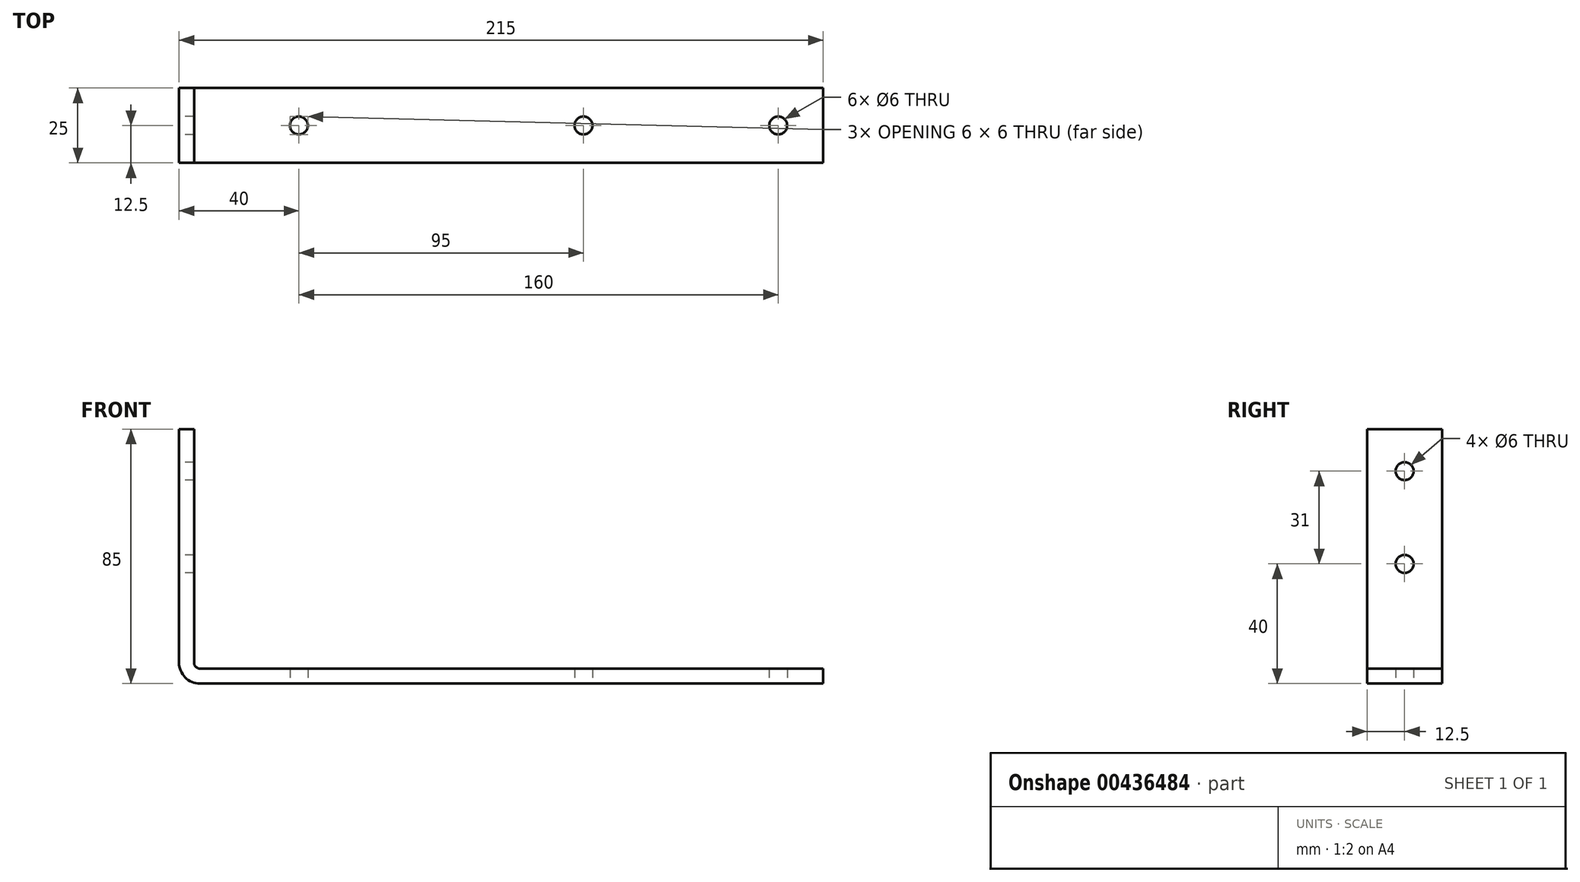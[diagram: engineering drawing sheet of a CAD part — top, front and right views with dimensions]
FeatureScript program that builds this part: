
annotation { "Feature Type Name" : "Feature", "Feature Type Description" : "" }
export const myFeature = defineFeature(function(context is Context, id is Id, definition is map)
    precondition{}
    {
        {
            var Q0;
            Q0=qCreatedBy(makeId("Front.planeOp"),FACE);
            var sketch = newSketch(context, id + "F0", { "sketchPlane" : qUnion([Q0])});
            skLineSegment(sketch, "E0.bottom", {"start": v(0, 85) * mm, "end": v(5, 85) * mm});
            skLineSegment(sketch, "E0.top", {"start": v(7, 0) * mm, "end": v(215, 0) * mm});
            skLineSegment(sketch, "E0.left", {"start": v(0, 85) * mm, "end": v(0, 7) * mm});
            skLineSegment(sketch, "E0.right", {"start": v(215, 5) * mm, "end": v(215, 0) * mm});
            skLineSegment(sketch, "E1.top", {"start": v(7, 5) * mm, "end": v(215, 5) * mm});
            skLineSegment(sketch, "E1.left", {"start": v(5, 85) * mm, "end": v(5, 7) * mm});
            skPoint(sketch, "E2.visualSharp", {"position": v(0, 0) * mm});
            skArc(sketch, "E2.filletArc", {"start": v(0, 7) * mm, "mid": v(2.05, 2.05) * mm, "end": v(7, 0) * mm});
            skPoint(sketch, "E3.visualSharp", {"position": v(5, 5) * mm});
            skArc(sketch, "E3.filletArc", {"start": v(5, 7) * mm, "mid": v(5.59, 5.59) * mm, "end": v(7, 5) * mm});
            skSolve(sketch);
        }
        {
            var Q0;
            Q0 = qSketchRegion(id + "F0", true);
            extrude(context, id + "F1", {"entities" : qUnion([Q0]), "depth" : 12.5 * mm, "hasSecondDirection" : true, "secondDirectionOppositeDirection" : true, "secondDirectionDepth" : 12.5 * mm});
        }
        {
            var Q0;
            Q0=makeQuery(id+"F1.opExtrude","SWEPT_FACE",FACE,{"disambiguationData":[OSD([sQuery(id+"F0.wireOp",EDGE,"E0.top")])]});
            var sketch = newSketch(context, id + "F2", { "sketchPlane" : qUnion([Q0])});
            skPoint(sketch, "E4", {"position": v(40, 0) * mm});
            skPoint(sketch, "E4.positionSnap0", {"position": v(7, 0) * mm});
            skPoint(sketch, "E5", {"position": v(135, 0) * mm});
            skPoint(sketch, "E6", {"position": v(200, 0) * mm});
            skSolve(sketch);
        }
        {
            var Q0;
            Q0=makeQuery(id+"F1.opExtrude","SWEPT_FACE",FACE,{"disambiguationData":[OSD([sQuery(id+"F0.wireOp",EDGE,"E0.left")])]});
            var sketch = newSketch(context, id + "F3", { "sketchPlane" : qUnion([Q0])});
            skPoint(sketch, "E7", {"position": v(0, 40) * mm});
            skPoint(sketch, "E8", {"position": v(0, 71) * mm});
            skSolve(sketch);
        }
        {
            var Q0;
            Q0=sQuery(id+"F2.wireOp",VERTEX,"E6");
            var Q1;
            Q1=sQuery(id+"F2.wireOp",VERTEX,"E5");
            var Q2;
            Q2=sQuery(id+"F2.wireOp",VERTEX,"E4");
            var Q3;
            Q3=sQuery(id+"F3.wireOp",VERTEX,"E7");
            var Q4;
            Q4=sQuery(id+"F3.wireOp",VERTEX,"E8");
            var Q5;
            Q5=makeQuery(id+"F1.opExtrude","SWEPT_BODY",BODY,{"disambiguationData":[OSD([sQuery(id+"F0.wireOp",EDGE,"E0.bottom"),sQuery(id+"F0.wireOp",EDGE,"E0.top"),sQuery(id+"F0.wireOp",EDGE,"E0.left"),sQuery(id+"F0.wireOp",EDGE,"E0.right"),sQuery(id+"F0.wireOp",EDGE,"E1.top"),sQuery(id+"F0.wireOp",EDGE,"E1.left"),sQuery(id+"F0.wireOp",EDGE,"E2.filletArc"),sQuery(id+"F0.wireOp",EDGE,"E3.filletArc")])]});
            hole(context, id + "F4", {"style" : HoleStyle.SIMPLE, "endStyle" : HoleEndStyle.THROUGH, "holeDiameter" : 6 * mm, "isTappedThrough" : true, "tappedDepth" : 12 * mm, "tapClearance" : 3, "locations" : qUnion([Q0, Q1, Q2, Q3, Q4]), "scope" : qUnion([Q5])});
        }
    });
